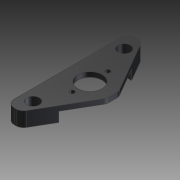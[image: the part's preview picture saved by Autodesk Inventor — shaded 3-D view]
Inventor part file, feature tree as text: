
AUTODESK INVENTOR PART (.ipt)
format: ipt  version: 2014 SP1 (Build 180222100, 222)  size: 120,832 bytes
history: native  units: in
note: dims shown in document units (in); Inventor stores cm internally (conversion verified against a paired STEP export)
features: fillet x1, other x1, imported_body x1
ambient origin geometry x8: Origin, YZ Plane, XZ Plane, XY Plane, X Axis, Y Axis, Z Axis, Center Point
bodies: Body1 (feature_tree)
feature tree (3):
  fillet  "Fillet6"  [1 undecoded]
  other  "encoder bracket.ipt1"
  imported_body  "Base1"
note: 1 required parameter value undecoded (feature->parameter linkage not recoverable at this tier; creation-order binding heuristic only, values carry confidence <= 0.55)
